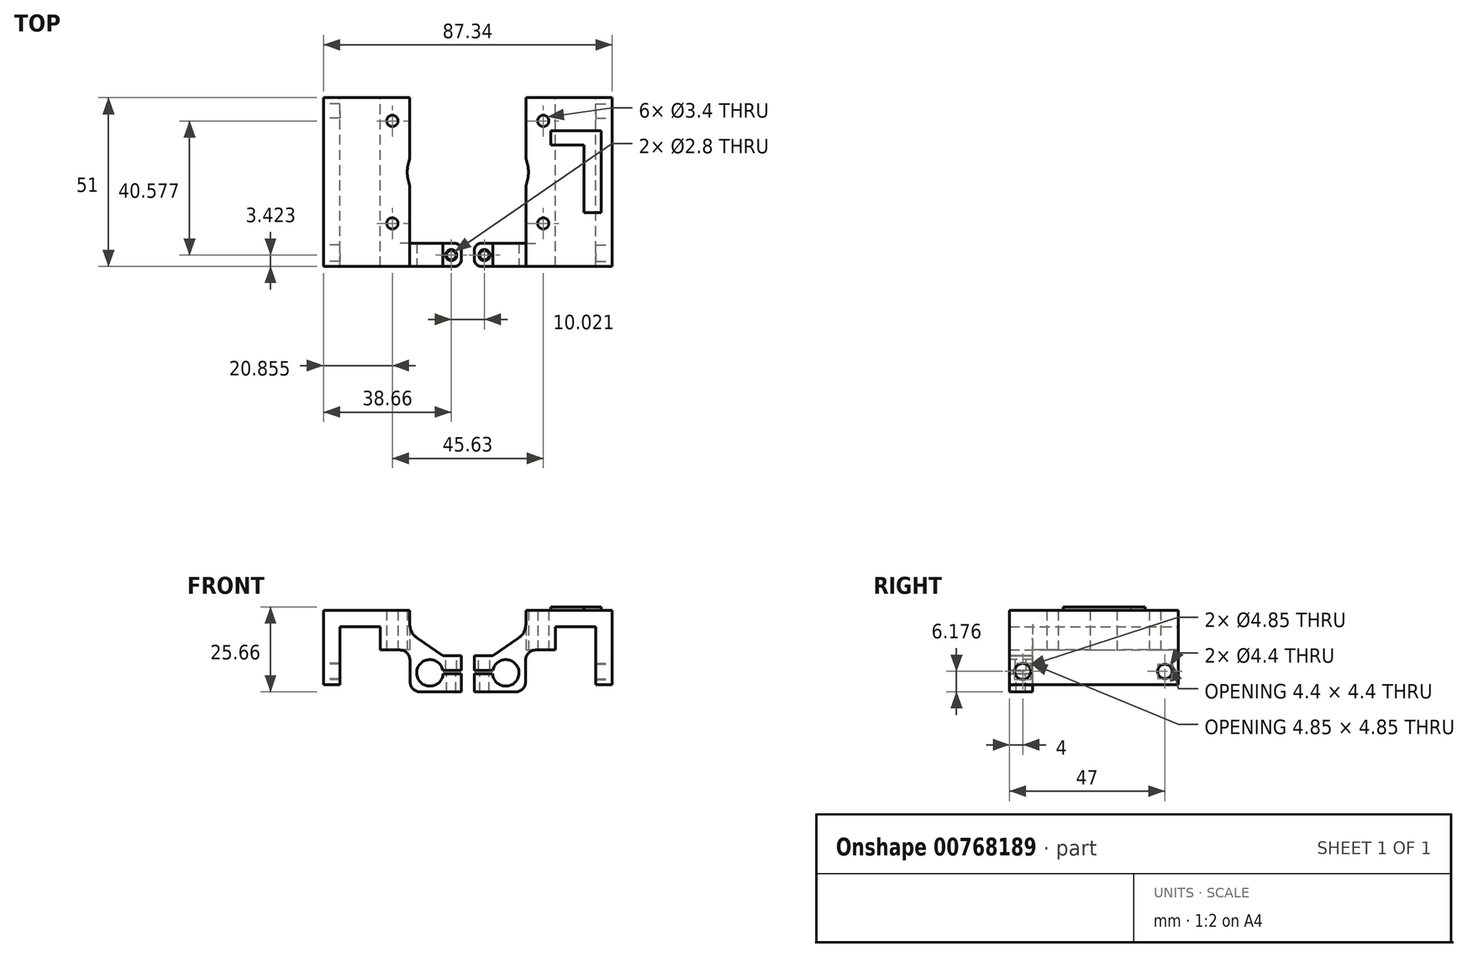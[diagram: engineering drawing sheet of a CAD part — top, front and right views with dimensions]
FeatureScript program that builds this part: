
annotation { "Feature Type Name" : "Feature", "Feature Type Description" : "" }
export const myFeature = defineFeature(function(context is Context, id is Id, definition is map)
    precondition{}
    {
        {
            var Q0;
            Q0=qCreatedBy(makeId("Front.planeOp"),FACE);
            var sketch = newSketch(context, id + "F0", { "sketchPlane" : qUnion([Q0])});
            skLineSegment(sketch, "E0", {"start": v(-18.67, 7.33) * mm, "end": v(-18.67, 29.8) * mm});
            skLineSegment(sketch, "E1", {"start": v(-18.67, 29.8) * mm, "end": v(7.46, 29.8) * mm});
            skLineSegment(sketch, "E2", {"start": v(7.46, 29.8) * mm, "end": v(7.46, 22.94) * mm});
            skLineSegment(sketch, "E3", {"start": v(-1.47, 17.8) * mm, "end": v(-1.47, 24.8) * mm});
            skLineSegment(sketch, "E4", {"start": v(-1.47, 24.8) * mm, "end": v(-13.67, 24.8) * mm});
            skLineSegment(sketch, "E5", {"start": v(-13.67, 24.8) * mm, "end": v(-13.67, 7.33) * mm});
            skLineSegment(sketch, "E6", {"start": v(-13.67, 7.33) * mm, "end": v(-18.67, 7.33) * mm});
            skLineSegment(sketch, "E7", {"start": v(7.46, 22.94) * mm, "end": v(7.46, 17.8) * mm});
            skLineSegment(sketch, "E8", {"start": v(7.46, 17.8) * mm, "end": v(-1.47, 17.8) * mm});
            skLineSegment(sketch, "E9", {"start": v(7.46, 22.94) * mm, "end": v(7.46, 22.94) * mm});
            skLineSegment(sketch, "E10", {"start": v(22.99, 16.14) * mm, "end": v(22.99, 11.7) * mm});
            skLineSegment(sketch, "E11", {"start": v(22.99, 11.7) * mm, "end": v(15.69, 11.7) * mm});
            skLineSegment(sketch, "E12", {"start": v(15.69, 11.7) * mm, "end": v(15.69, 10.67) * mm});
            skLineSegment(sketch, "E13", {"start": v(15.69, 10.67) * mm, "end": v(23.02, 10.67) * mm});
            skLineSegment(sketch, "E14", {"start": v(23.02, 10.67) * mm, "end": v(23.02, 5.15) * mm});
            skLineSegment(sketch, "E15", {"start": v(23.02, 5.15) * mm, "end": v(7.6, 5.15) * mm});
            skLineSegment(sketch, "E16", {"start": v(7.6, 5.15) * mm, "end": v(7.46, 17.8) * mm});
            skLineSegment(sketch, "E17", {"start": v(22.99, 16.14) * mm, "end": v(17.43, 16.14) * mm});
            skLineSegment(sketch, "E18", {"start": v(17.43, 16.14) * mm, "end": v(7.46, 22.94) * mm});
            skSolve(sketch);
        }
        {
            var Q0;
            Q0=makeQuery(id+"F0.imprint","IMPRINT",FACE,{"disambiguationData":[TD([[makeQuery(id+"F0.imprint","IMPRINT",EDGE,{"derivedFrom":sQuery(id+"F0.wireOp",EDGE,"E0")}),-1.0]])]});
            var Q1;
            {var subQ2=sQuery(id+"F0.wireOp",EDGE,"69cbcc5d-e0c3-48db-8baf-3487a8abab7d");Q1=makeQuery(id+"F0.imprint","IMPRINT",FACE,{"disambiguationData":[TD([[makeQuery(id+"F0.imprint","IMPRINT",EDGE,{"derivedFrom":subQ2}),-1.0]])]});}
            var Q2;
            Q2=makeQuery(id+"F0.imprint","IMPRINT",FACE,{"disambiguationData":[TD([[makeQuery(id+"F0.imprint","IMPRINT",EDGE,{"derivedFrom":sQuery(id+"F0.wireOp",EDGE,"E7")}),1.0]])]});
            extrude(context, id + "F1", {"entities" : qUnion([Q0, Q1, Q2]), "depth" : 7 * mm});
        }
        {
            var Q0;
            Q0=makeQuery(id+"F0.imprint","IMPRINT",FACE,{"disambiguationData":[TD([[makeQuery(id+"F0.imprint","IMPRINT",EDGE,{"derivedFrom":sQuery(id+"F0.wireOp",EDGE,"E0")}),-1.0]])]});
            extrude(context, id + "F2", {"entities" : qUnion([Q0]), "operationType" : NewBodyOperationType.ADD, "oppositeDirection" : true, "depth" : 44 * mm, "offsetDistance" : 25 * mm});
        }
        {
            var Q0;
            {var subQ0=sQuery(id+"F0.wireOp",EDGE,"E8");Q0=makeQuery(id+"F2.boolean.opBoolean","MERGE",FACE,{"derivedFrom":[makeQuery(id+"F1.opExtrude","SWEPT_FACE",FACE,{"disambiguationData":[OSD([subQ0])]}),makeQuery(id+"F2.opExtrude","SWEPT_FACE",FACE,{"disambiguationData":[OSD([subQ0])]})]});}
            var sketch = newSketch(context, id + "F3", { "sketchPlane" : qUnion([Q0])});
            skCircle(sketch, "E19", {"center": v(2.19, -6) * mm, "radius": 1.7 * mm});
            skCircle(sketch, "E20", {"center": v(2.19, -37) * mm, "radius": 1.7 * mm});
            skCircle(sketch, "E21", {"center": v(17.69, -21.5) * mm, "radius": 11 * mm});
            skSolve(sketch);
        }
        {
            var Q0;
            Q0=qSketchRegion(id+"F3",true);
            extrude(context, id + "F4", {"entities" : qUnion([Q0]), "operationType" : NewBodyOperationType.REMOVE, "endBound" : BoundingType.THROUGH_ALL, "oppositeDirection" : true, "depth" : 25 * mm});
        }
        {
            var Q0;
            Q0=makeQuery(id+"F1.opExtrude","CAP_FACE",FACE,{"disambiguationData":[OSD([sQuery(id+"F0.wireOp",EDGE,"E0"),sQuery(id+"F0.wireOp",EDGE,"E1"),sQuery(id+"F0.wireOp",EDGE,"E2"),sQuery(id+"F0.wireOp",EDGE,"E3"),sQuery(id+"F0.wireOp",EDGE,"E4"),sQuery(id+"F0.wireOp",EDGE,"E5"),sQuery(id+"F0.wireOp",EDGE,"E6"),sQuery(id+"F0.wireOp",EDGE,"E8"),sQuery(id+"F0.wireOp",EDGE,"E9"),sQuery(id+"F0.wireOp",EDGE,"58f11638-63e7-4b32-8aff-a1ba3c53649b"),sQuery(id+"F0.wireOp",EDGE,"E10"),sQuery(id+"F0.wireOp",EDGE,"E11"),sQuery(id+"F0.wireOp",EDGE,"E12"),sQuery(id+"F0.wireOp",EDGE,"E13"),sQuery(id+"F0.wireOp",EDGE,"E14"),sQuery(id+"F0.wireOp",EDGE,"E15"),sQuery(id+"F0.wireOp",EDGE,"E16")])],"isStart":false});
            var sketch = newSketch(context, id + "F5", { "sketchPlane" : qUnion([Q0])});
            skCircle(sketch, "E22", {"center": v(13.53, 10.9) * mm, "radius": 4 * mm});
            skSolve(sketch);
        }
        {
            var Q0;
            Q0=qSketchRegion(id+"F5",true);
            extrude(context, id + "F6", {"entities" : qUnion([Q0]), "operationType" : NewBodyOperationType.REMOVE, "oppositeDirection" : true, "depth" : 10 * mm});
        }
        {
            var Q0;
            Q0=qSketchRegion(id+"F3",true);
            extrude(context, id + "F7", {"entities" : qUnion([Q0]), "operationType" : NewBodyOperationType.REMOVE, "endBound" : BoundingType.THROUGH_ALL, "oppositeDirection" : true, "depth" : 25 * mm});
        }
        {
            var Q0;
            Q0=makeQuery(id+"F1.opExtrude","SWEPT_FACE",FACE,{"disambiguationData":[OSD([sQuery(id+"F0.wireOp",EDGE,"E17")])]});
            var sketch = newSketch(context, id + "F8", { "sketchPlane" : qUnion([Q0])});
            skCircle(sketch, "E23", {"center": v(19.99, -3.58) * mm, "radius": 1.7 * mm});
            skCircle(sketch, "E24", {"center": v(19.99, -3.58) * mm, "radius": 1.4 * mm});
            skSolve(sketch);
        }
        {
            var Q0;
            Q0=makeQuery(id+"F8.imprint","IMPRINT",FACE,{"disambiguationData":[TD([[makeQuery(id+"F8.imprint","IMPRINT",EDGE,{"derivedFrom":sQuery(id+"F8.wireOp",EDGE,"E24")}),1.0]])]});
            extrude(context, id + "F9", {"entities" : qUnion([Q0]), "operationType" : NewBodyOperationType.REMOVE, "endBound" : BoundingType.THROUGH_ALL, "oppositeDirection" : true, "depth" : 25 * mm});
        }
        {
            var Q0;
            Q0=makeQuery(id+"F8.imprint","IMPRINT",FACE,{"disambiguationData":[TD([[makeQuery(id+"F8.imprint","IMPRINT",EDGE,{"derivedFrom":sQuery(id+"F8.wireOp",EDGE,"E23")}),1.0]])]});
            extrude(context, id + "F10", {"entities" : qUnion([Q0]), "operationType" : NewBodyOperationType.REMOVE, "endBound" : BoundingType.UP_TO_NEXT, "oppositeDirection" : true, "depth" : 25 * mm});
        }
        {
            var Q0;
            Q0=makeQuery(id+"F1.opExtrude","SWEPT_EDGE",EDGE,{"disambiguationData":[OSD([sQuery(id+"F0.wireOp",EDGE,"E2"),sQuery(id+"F0.wireOp",EDGE,"E7"),sQuery(id+"F0.wireOp",EDGE,"E18")])]});
            fillet(context, id + "F11", {"entities" : qUnion([Q0]), "radius" : 5 * mm, "tangentPropagation" : true, "allowEdgeOverflow" : false});
        }
        {
            var Q0;
            Q0=makeQuery(id+"F1.opExtrude","SWEPT_EDGE",EDGE,{"disambiguationData":[OSD([sQuery(id+"F0.wireOp",EDGE,"E7"),sQuery(id+"F0.wireOp",EDGE,"E8"),sQuery(id+"F0.wireOp",EDGE,"E16")])]});
            fillet(context, id + "F12", {"entities" : qUnion([Q0]), "radius" : 3 * mm, "tangentPropagation" : true, "allowEdgeOverflow" : false});
        }
        {
            var Q0;
            Q0=makeQuery(id+"F1.opExtrude","SWEPT_EDGE",EDGE,{"disambiguationData":[OSD([sQuery(id+"F0.wireOp",EDGE,"E15"),sQuery(id+"F0.wireOp",EDGE,"E16")])]});
            fillet(context, id + "F13", {"entities" : qUnion([Q0]), "radius" : 3 * mm, "tangentPropagation" : true, "allowEdgeOverflow" : false});
        }
        {
            var Q0;
            Q0=makeQuery(id+"F1.opExtrude","CAP_EDGE",EDGE,{"disambiguationData":[OSD([sQuery(id+"F0.wireOp",EDGE,"E10")])],"isStart":false});
            var Q1;
            Q1=makeQuery(id+"F1.opExtrude","CAP_EDGE",EDGE,{"disambiguationData":[OSD([sQuery(id+"F0.wireOp",EDGE,"E14")])],"isStart":false});
            var Q2;
            Q2=makeQuery(id+"F1.opExtrude","CAP_EDGE",EDGE,{"disambiguationData":[OSD([sQuery(id+"F0.wireOp",EDGE,"E10")])],"isStart":true});
            var Q3;
            Q3=makeQuery(id+"F1.opExtrude","CAP_EDGE",EDGE,{"disambiguationData":[OSD([sQuery(id+"F0.wireOp",EDGE,"E14")])],"isStart":true});
            fillet(context, id + "F14", {"entities" : qUnion([Q0, Q1, Q2, Q3]), "radius" : 2 * mm, "tangentPropagation" : true, "allowEdgeOverflow" : false});
        }
        {
            var Q0;
            {var subQ0=sQuery(id+"F0.wireOp",EDGE,"E0");Q0=makeQuery(id+"F2.boolean.opBoolean","MERGE",FACE,{"derivedFrom":[makeQuery(id+"F1.opExtrude","SWEPT_FACE",FACE,{"disambiguationData":[OSD([subQ0])]}),makeQuery(id+"F2.opExtrude","SWEPT_FACE",FACE,{"disambiguationData":[OSD([subQ0])]})]});}
            var sketch = newSketch(context, id + "F15", { "sketchPlane" : qUnion([Q0])});
            skCircle(sketch, "E25", {"center": v(-40, 11.33) * mm, "radius": 2.2 * mm});
            skCircle(sketch, "E26", {"center": v(3, 11.33) * mm, "radius": 2.43 * mm});
            skSolve(sketch);
        }
        {
            var Q0;
            Q0=qSketchRegion(id+"F15",true);
            extrude(context, id + "F16", {"entities" : qUnion([Q0]), "operationType" : NewBodyOperationType.REMOVE, "oppositeDirection" : true, "depth" : 6 * mm});
        }
        {
            var Q0;
            Q0=makeQuery(id+"F1.opExtrude","SWEPT_BODY",BODY,{"disambiguationData":[OSD([sQuery(id+"F0.wireOp",EDGE,"E0"),sQuery(id+"F0.wireOp",EDGE,"E1"),sQuery(id+"F0.wireOp",EDGE,"E2"),sQuery(id+"F0.wireOp",EDGE,"E3"),sQuery(id+"F0.wireOp",EDGE,"E4"),sQuery(id+"F0.wireOp",EDGE,"E5"),sQuery(id+"F0.wireOp",EDGE,"E6"),sQuery(id+"F0.wireOp",EDGE,"E8"),sQuery(id+"F0.wireOp",EDGE,"E10"),sQuery(id+"F0.wireOp",EDGE,"E11"),sQuery(id+"F0.wireOp",EDGE,"E12"),sQuery(id+"F0.wireOp",EDGE,"E13"),sQuery(id+"F0.wireOp",EDGE,"E14"),sQuery(id+"F0.wireOp",EDGE,"E15"),sQuery(id+"F0.wireOp",EDGE,"E16"),sQuery(id+"F0.wireOp",EDGE,"E17"),sQuery(id+"F0.wireOp",EDGE,"E18")])]});
            var Q1;
            Q1=qCreatedBy(makeId("Right.planeOp"),FACE);
            mirror(context, id + "F17", {"entities" : qUnion([Q0]), "mirrorPlane" : qUnion([Q1])});
        }
        {
            var Q0;
            Q0=makeQuery(id+"F17.opPattern","COPY",BODY,{"derivedFrom":makeQuery(id+"F1.opExtrude","SWEPT_BODY",BODY,{"disambiguationData":[OSD([sQuery(id+"F0.wireOp",EDGE,"E0"),sQuery(id+"F0.wireOp",EDGE,"E1"),sQuery(id+"F0.wireOp",EDGE,"E2"),sQuery(id+"F0.wireOp",EDGE,"E3"),sQuery(id+"F0.wireOp",EDGE,"E4"),sQuery(id+"F0.wireOp",EDGE,"E5"),sQuery(id+"F0.wireOp",EDGE,"E6"),sQuery(id+"F0.wireOp",EDGE,"E8"),sQuery(id+"F0.wireOp",EDGE,"E10"),sQuery(id+"F0.wireOp",EDGE,"E11"),sQuery(id+"F0.wireOp",EDGE,"E12"),sQuery(id+"F0.wireOp",EDGE,"E13"),sQuery(id+"F0.wireOp",EDGE,"E14"),sQuery(id+"F0.wireOp",EDGE,"E15"),sQuery(id+"F0.wireOp",EDGE,"E16"),sQuery(id+"F0.wireOp",EDGE,"E17"),sQuery(id+"F0.wireOp",EDGE,"E18")])]}),"instanceName":"1"});
            transform(context, id + "F18", {"entities" : qUnion([Q0]), "transformType" : TransformType.TRANSLATION_3D, "dx" : 50 * mm, "dy" : 0 * mm, "dz" : 0 * mm, "makeCopy" : false});
        }
        {
            var Q0;
            {var subQ0=sQuery(id+"F0.wireOp",EDGE,"E1");Q0=makeQuery(id+"F17.opPattern","COPY",FACE,{"derivedFrom":makeQuery(id+"F2.boolean.opBoolean","MERGE",FACE,{"derivedFrom":[makeQuery(id+"F1.opExtrude","SWEPT_FACE",FACE,{"disambiguationData":[OSD([subQ0])]}),makeQuery(id+"F2.opExtrude","SWEPT_FACE",FACE,{"disambiguationData":[OSD([subQ0])]})]}),"instanceName":"1"});}
            var sketch = newSketch(context, id + "F19", { "sketchPlane" : qUnion([Q0])});
            skText(sketch, "E27", { "text": "L", "fontName": "OpenSans-Bold.ttf"});
            skLineSegment(sketch, "E28", {"start": v(47.81, 37) * mm, "end": v(47.81, 6) * mm, "construction": true});
            skPoint(sketch, "E29", {"position": v(47.81, 21.5) * mm});
            const initialGuessF19  = {"E27": [0.0685, 0.034, -1, 0, 0.025]};
            skSetInitialGuess(sketch, initialGuessF19);
            skSolve(sketch);
        }
        {
            var Q0;
            Q0 = qSketchRegion(id + "F19", true);
            extrude(context, id + "F20", {"entities" : qUnion([Q0]), "operationType" : NewBodyOperationType.ADD, "depth" : 1 * mm, "offsetDistance" : 25 * mm});
        }
    });
